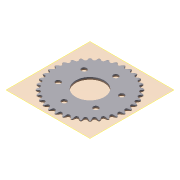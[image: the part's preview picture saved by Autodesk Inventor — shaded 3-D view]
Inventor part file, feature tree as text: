
AUTODESK INVENTOR PART (.ipt)
format: ipt  version: 2011 (Build 150239000, 239)  size: 883,200 bytes
history: native  units: mm
features: other x7, extrude x3, sketch x2, pattern_linear x1, pattern_circular x1, hole x1
ambient origin geometry x8: Origin, YZ Plane, XZ Plane, XY Plane, X Axis, Y Axis, Z Axis, Center Point
bodies: Solid1 (feature_tree)
feature tree (15):
  other  "25 sprocket 36T"
  other  "Theoretical Tooth Profile"
  other  "Tooth Profile"
  other  "Section Profile"
  other  "Shroud"
  other  "Strand"
  pattern_linear  "Strand Pattern"  Spacing1=1.697355mm  [1 undecoded]
  extrude  "Theoretical Tooth"  Depth=22.107504mm
  extrude  "Tooth"  Depth=2.870097mm
  pattern_circular  "Tooth Pattern"  [2 undecoded]
  other  "Timing Plane"
  extrude  "Extrusion4"  Depth=4.338955mm
  hole  "Hole1"  [1 undecoded]
  sketch  "Sketch4"  dims[d0=72.858079mm]
  sketch  "Sketch5"  dims[d2=1.745329mm d3=1.697355mm d10=22.107504mm d11=2.870097mm d12=2.6416mm d13=4.338955mm d14=4.6228mm d18=10.0mm d19=0.0mm d20=360.0mm d21=360.0deg d23=1.905mm d28=0.0mm d29=0.0mm d30=2.286mm d31=64.960832mm d32=2.286mm d33=0.79375mm d34=6.75005mm d36=90.0deg d37=90.0deg d38=10.0mm d40=6.4008mm d42=0.0mm d43=1.143mm d44=23.998278mm d45=1.697355mm d46=15.05712mm d47=0.0mm d48=25.4mm d49=0.0mm d50=10.0mm d51=28.5623mm d52=25.4mm d53=0.0mm d54=47.625mm d55=60.0mm d57=360.0deg d59=5.2324mm d60=19.05mm d61=9.525mm d62=6.35mm d63=14.3117mm d64=25.4mm d65=20.594885mm]
note: 4 required parameter values undecoded (feature->parameter linkage not recoverable at this tier; creation-order binding heuristic only, values carry confidence <= 0.55)
